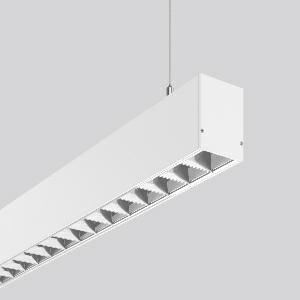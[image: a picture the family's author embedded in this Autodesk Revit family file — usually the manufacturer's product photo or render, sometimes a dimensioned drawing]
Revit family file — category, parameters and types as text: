
# Revit family: less_is_more_50_312342_002_1_baf6
name_source: partatom
category: Lighting Fixtures
units: mm (PartAtom-declared; Revit-internal decimal feet)

## family parameters
Cut with Voids When Loaded = No
Host = Face
Light Source = No
Part Type = Normal
Room Calculation Point = No
Round Connector Dimension = Use Diameter
Shared = No

## types (1)
- LESS IS MORE 50 (1 x LED Modul 840, 5050 lm, 4000)
    Apparent Load = 46 VA
    CIE Flux Codes = 95 100 100 63 100
    Color Rendering = 80
    Color Temperature = 4000
    Default Elevation = 1800 mm
    Description = Series: LESS IS MORE 50
Linear pendant luminaire for aesthetically sophisticated lighting. Housing: extruded aluminium profile, powder-coated. End cap aluminium powder-coated. Canopy made of aluminium, powder-coated. Alea optical system: Reflector structure (ABS, Aluminium-coated, highly polished) with integrated diffuser made of non-yellowing plastic (PMMA) opal for glare-free light at the workstation (screen-compliant according to EN 12464-1). Direct 65%, indirect 35% light emission. Suitable for pendant. 2-point steel cable suspension freely positionable and infinitely height-adjustable. Special lengths available on request. LED unit with integrated converter interchangeable and removable. Suitable for through-wiring. With sensors or as a safety luminaire on request. 
Colour: traffic white, matt (RAL 9016)
Length: 1127 mm
Width: 57 mm
Height: 75 mm
Suspension length: 2000 mm
Lamp: LED
Socket: without socket
Colour temperature: 4000K
Colour rendering index (CRI): 80
Light source: LED
Socket lamp2: Without base
Colour temperature: 4000K
System power: 46 W
Rated luminous flux: 5050 lm
Luminous efficiency: 110 lm/W
Control gear: Regulated power supply
Control gear: Regulated power supply
Protection class: I
Type of protection: IP 20
    Height = 75 mm
    Lamp = 1 x LED Modul 840
    Lamp Light Flux = 5050 lm
    Lamp count = 1
    Length = 1127 mm
    Lifetime = 50000 h
    Luminous efficacy = 110 lm/W
    Manufacturer = RZB
    ModVariant = No
    Model = 312342.002.1
    Mounting Place = Ceiling
    Mounting Type = Pendant
    Number of Poles = 1
    OnlyDefault = Yes
    Power Factor = 1
    Product Name = LESS IS MORE 50
    Product group = Pendant LED linear luminaires
    ProductGroupID = 907
    Protection Class = Protection class I
    Protection Degree = IP 20
    RLX_Detail_Level = 1
    RLX_Emergency_Light_Flux = 0 lm
    RLX_Emergency_Type = 0
    RLX_Emergency_Type_DB = No
    RlxData = <blob elided: 37457 chars, md5=56c9f9ba>
    Socket = socket
    Standby Power = 0 W
    System Light Flux = 5050 lm
    System Power = 46 W
    Type Comments = Product without accessories
    Type Image = 312342.002.jpg
    URL = http://relux.com
    VarID = ---
    Voltage = 230 V
    Voltage Range = 220-240 V
    Weight = 0.00 kg
    Width = 57 mm

## geometry (parser evidence)
native form markers: Blend x4, Sweep x12
no freeform markers — native parametric forms only
